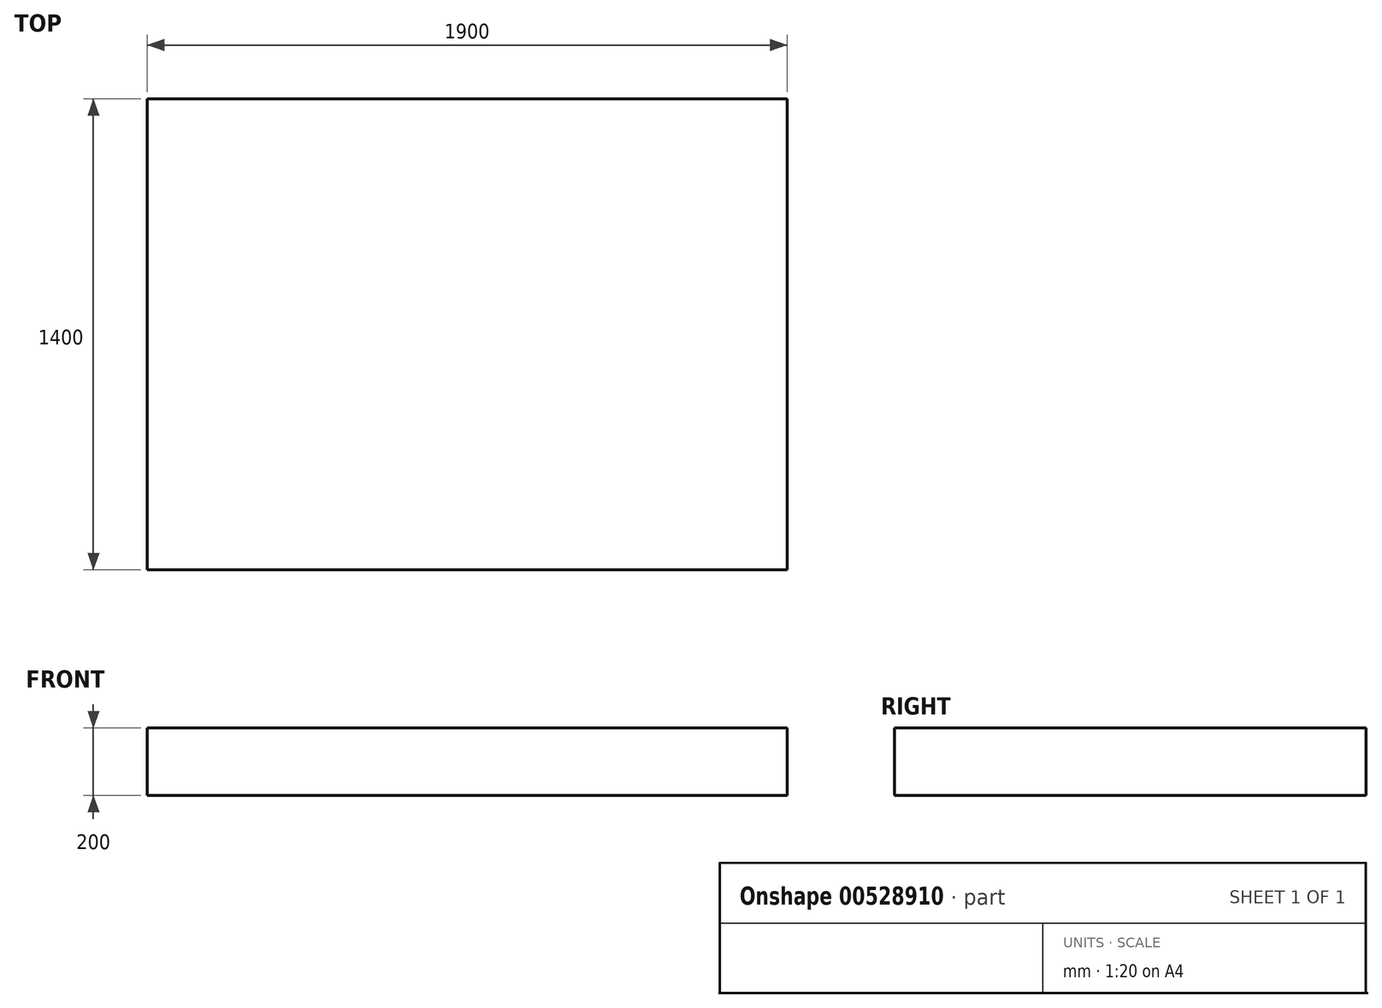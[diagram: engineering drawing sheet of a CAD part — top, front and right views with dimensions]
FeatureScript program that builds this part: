
annotation { "Feature Type Name" : "Feature", "Feature Type Description" : "" }
export const myFeature = defineFeature(function(context is Context, id is Id, definition is map)
    precondition{}
    {
        {
            var Q0;
            Q0=qCreatedBy(makeId("Top.planeOp"),FACE);
            var sketch = newSketch(context, id + "F0", { "sketchPlane" : qUnion([Q0])});
            skLineSegment(sketch, "E0.bottom", {"start": v(0, 0) * mm, "end": v(1900, 0) * mm});
            skLineSegment(sketch, "E0.top", {"start": v(0, 1400) * mm, "end": v(1900, 1400) * mm});
            skLineSegment(sketch, "E0.left", {"start": v(0, 0) * mm, "end": v(0, 1400) * mm});
            skLineSegment(sketch, "E0.right", {"start": v(1900, 0) * mm, "end": v(1900, 1400) * mm});
            skSolve(sketch);
        }
        {
            var Q0;
            Q0=makeQuery(id+"F0.imprint","IMPRINT",FACE,{"disambiguationData":[TD([[makeQuery(id+"F0.imprint","IMPRINT",EDGE,{"derivedFrom":sQuery(id+"F0.wireOp",EDGE,"E0.bottom")}),1.0]])]});
            extrude(context, id + "F1", {"entities" : qUnion([Q0]), "depth" : 200 * mm, "offsetDistance" : 25 * mm});
        }
    });
